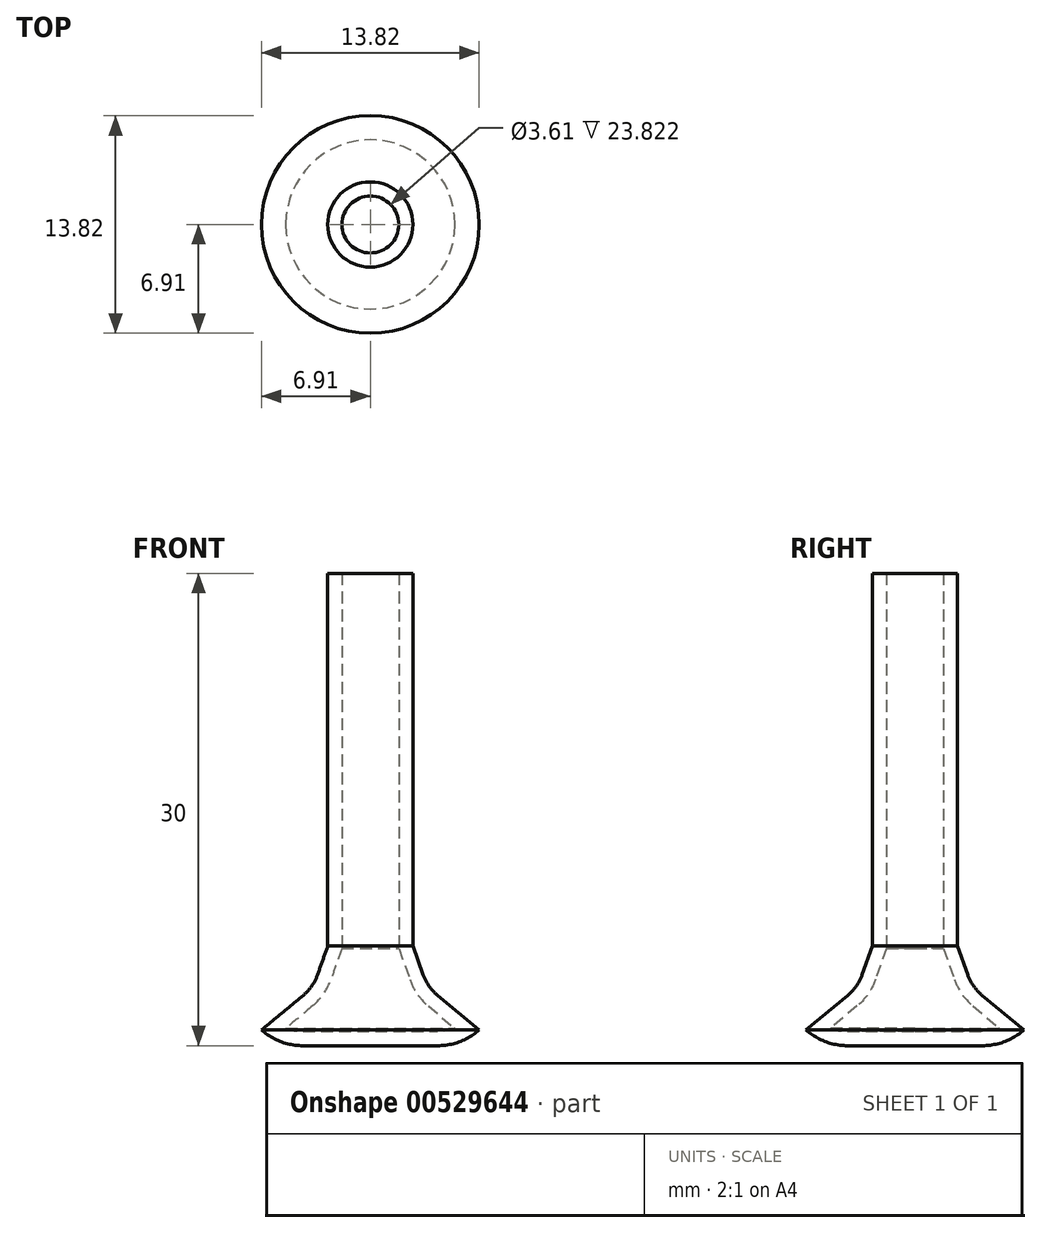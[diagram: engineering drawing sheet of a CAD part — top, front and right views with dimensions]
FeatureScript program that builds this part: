
annotation { "Feature Type Name" : "Feature", "Feature Type Description" : "" }
export const myFeature = defineFeature(function(context is Context, id is Id, definition is map)
    precondition{}
    {
        {
            var Q0;
            Q0=qCreatedBy(makeId("Front.planeOp"),FACE);
            var sketch = newSketch(context, id + "F0", { "sketchPlane" : qUnion([Q0])});
            skLineSegment(sketch, "E0", {"start": v(0, 0) * mm, "end": v(0, 30) * mm});
            skLineSegment(sketch, "E1", {"start": v(0, 30) * mm, "end": v(-2.7, 30) * mm});
            skLineSegment(sketch, "E2", {"start": v(-2.7, 30) * mm, "end": v(-2.7, 6.33) * mm});
            skLineSegment(sketch, "E3", {"start": v(-2.7, 6.33) * mm, "end": v(-3.35, 4.5) * mm});
            skLineSegment(sketch, "E4", {"start": v(-6.91, 0.99) * mm, "end": v(-4.26, 3.2) * mm});
            skPoint(sketch, "E5.visualSharp", {"position": v(-3.63, 3.73) * mm});
            skArc(sketch, "E5.filletArc", {"start": v(-4.26, 3.2) * mm, "mid": v(-3.72, 3.8) * mm, "end": v(-3.35, 4.5) * mm});
            skLineSegment(sketch, "E6", {"start": v(-6.91, 0.99) * mm, "end": v(-6.91, 0.99) * mm});
            skLineSegment(sketch, "E7", {"start": v(-4.28, 0) * mm, "end": v(0, 0) * mm});
            skPoint(sketch, "E8.visualSharp", {"position": v(-5.78, 0) * mm});
            skArc(sketch, "E8.filletArc", {"start": v(-6.91, 0.99) * mm, "mid": v(-5.68, 0.26) * mm, "end": v(-4.28, 0) * mm});
            skSolve(sketch);
        }
        {
            var Q0;
            Q0=makeQuery(id+"F0.imprint","IMPRINT",FACE,{"disambiguationData":[TD([[makeQuery(id+"F0.imprint","IMPRINT",EDGE,{"derivedFrom":sQuery(id+"F0.wireOp",EDGE,"E0")}),1.0]])]});
            var Q1;
            Q1=sQuery(id+"F0.wireOp",EDGE,"E0");
            revolve(context, id + "F1", {"entities" : qUnion([Q0]), "axis" : qUnion([Q1]), "revolveType" : RevolveType.FULL});
        }
        {
            var Q0;
            Q0=makeQuery(id+"F1.opRevolve","SWEPT_FACE",FACE,{"disambiguationData":[OSD([sQuery(id+"F0.wireOp",EDGE,"E1")])]});
            shell(context, id + "F2", {"entities" : qUnion([Q0]), "thickness" : 0.9 * mm});
        }
    });
